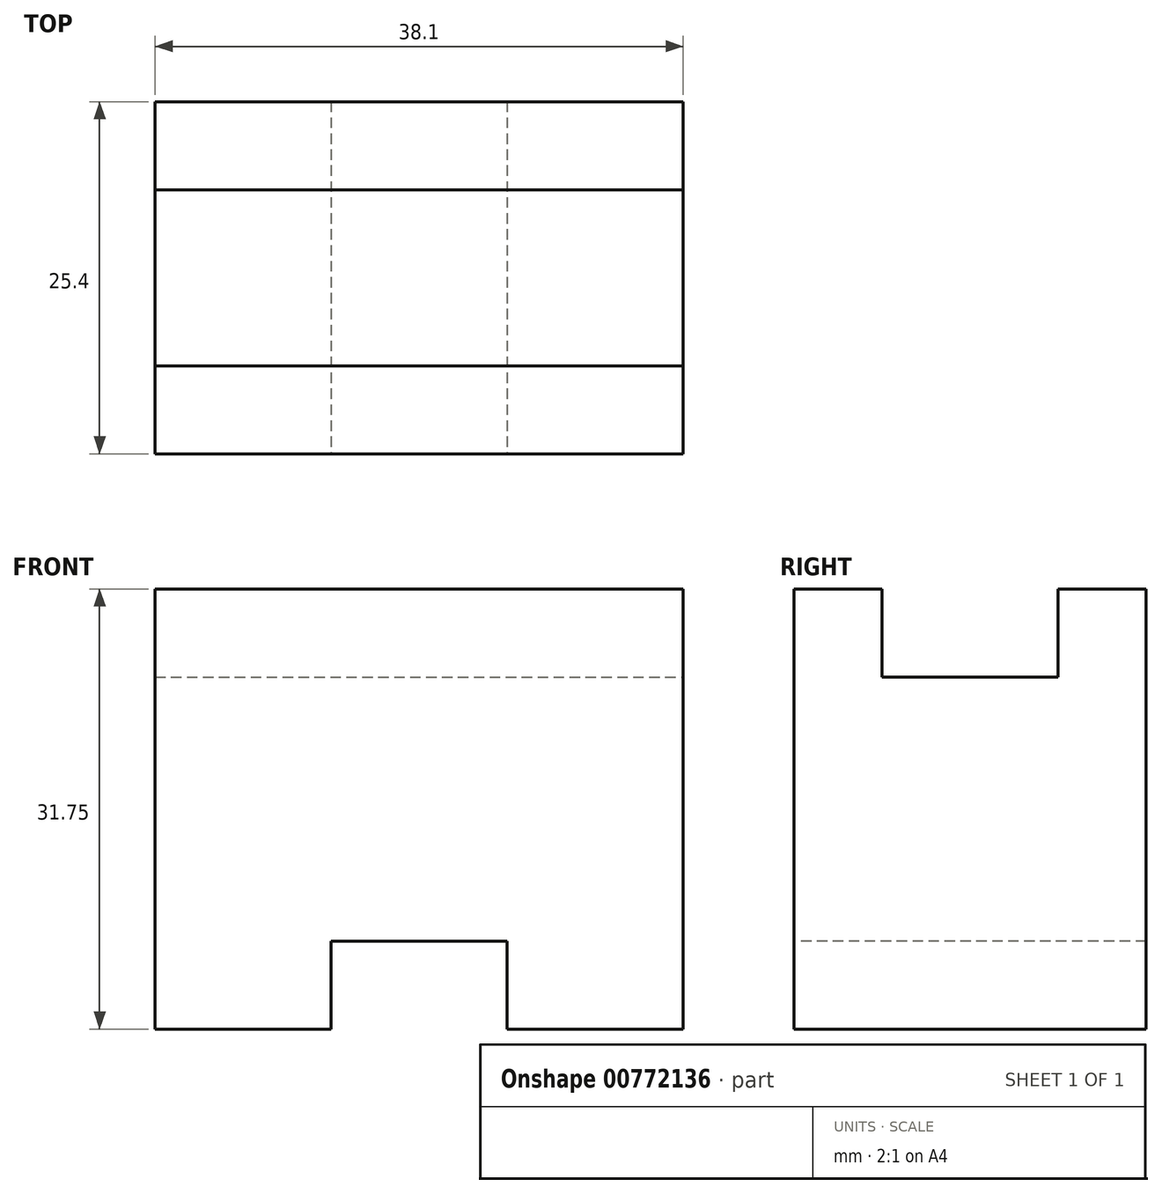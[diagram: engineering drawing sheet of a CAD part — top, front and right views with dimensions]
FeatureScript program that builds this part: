
annotation { "Feature Type Name" : "Feature", "Feature Type Description" : "" }
export const myFeature = defineFeature(function(context is Context, id is Id, definition is map)
    precondition{}
    {
        {
            var Q0;
            Q0=qCreatedBy(makeId("Front.planeOp"),FACE);
            var sketch = newSketch(context, id + "F0", { "sketchPlane" : qUnion([Q0])});
            skLineSegment(sketch, "E0", {"start": v(0, 0) * mm, "end": v(38.1, 0) * mm});
            skLineSegment(sketch, "E1", {"start": v(38.1, 0) * mm, "end": v(38.1, 31.75) * mm});
            skLineSegment(sketch, "E2", {"start": v(38.1, 31.75) * mm, "end": v(0, 31.75) * mm});
            skLineSegment(sketch, "E3", {"start": v(0, 31.75) * mm, "end": v(0, 0) * mm});
            skSolve(sketch);
        }
        {
            var Q0;
            Q0 = qSketchRegion(id + "F0", true);
            extrude(context, id + "F1", {"entities" : qUnion([Q0]), "depth" : 25.4 * mm, "offsetDistance" : 25.4 * mm});
        }
        {
            var Q0;
            Q0=makeQuery(id+"F1.opExtrude","CAP_FACE",FACE,{"disambiguationData":[OSD([sQuery(id+"F0.wireOp",EDGE,"E0"),sQuery(id+"F0.wireOp",EDGE,"E1"),sQuery(id+"F0.wireOp",EDGE,"E2"),sQuery(id+"F0.wireOp",EDGE,"E3")])],"isStart":false});
            var sketch = newSketch(context, id + "F2", { "sketchPlane" : qUnion([Q0])});
            skLineSegment(sketch, "E4", {"start": v(0, 0) * mm, "end": v(12.7, 0) * mm});
            skLineSegment(sketch, "E5", {"start": v(12.7, 0) * mm, "end": v(12.7, 6.35) * mm});
            skLineSegment(sketch, "E6", {"start": v(12.7, 6.35) * mm, "end": v(25.4, 6.35) * mm});
            skLineSegment(sketch, "E7", {"start": v(25.4, 6.35) * mm, "end": v(25.4, 0) * mm});
            skLineSegment(sketch, "E8", {"start": v(25.4, 0) * mm, "end": v(38.1, 0) * mm});
            skSolve(sketch);
        }
        {
            var Q0;
            {var subQ0=sQuery(id+"F2.wireOp",EDGE,"E5");Q0=makeQuery(id+"F2.imprint","IMPRINT",FACE,{"disambiguationData":[TD([[makeQuery(id+"F2.imprint","IMPRINT",EDGE,{"derivedFrom":subQ0}),-1.0]])]});}
            extrude(context, id + "F3", {"entities" : qUnion([Q0]), "operationType" : NewBodyOperationType.REMOVE, "oppositeDirection" : true, "depth" : 25.4 * mm, "offsetDistance" : 25.4 * mm});
        }
        {
            var Q0;
            Q0=makeQuery(id+"F1.opExtrude","SWEPT_FACE",FACE,{"disambiguationData":[OSD([sQuery(id+"F0.wireOp",EDGE,"E1")])]});
            var sketch = newSketch(context, id + "F4", { "sketchPlane" : qUnion([Q0])});
            skLineSegment(sketch, "E9", {"start": v(-25.4, 31.75) * mm, "end": v(-19.05, 31.75) * mm});
            skLineSegment(sketch, "E10", {"start": v(-19.05, 31.75) * mm, "end": v(-19.05, 25.4) * mm});
            skLineSegment(sketch, "E11", {"start": v(-19.05, 25.4) * mm, "end": v(-6.35, 25.4) * mm});
            skLineSegment(sketch, "E12", {"start": v(-6.35, 25.4) * mm, "end": v(-6.35, 31.75) * mm});
            skPoint(sketch, "E12.endSnap0", {"position": v(-22.23, 31.75) * mm});
            skLineSegment(sketch, "E13", {"start": v(-6.35, 31.75) * mm, "end": v(0, 31.75) * mm});
            skSolve(sketch);
        }
        {
            var Q0;
            {var subQ0=sQuery(id+"F4.wireOp",EDGE,"E10");Q0=makeQuery(id+"F4.imprint","IMPRINT",FACE,{"disambiguationData":[TD([[makeQuery(id+"F4.imprint","IMPRINT",EDGE,{"derivedFrom":subQ0}),1.0]])]});}
            extrude(context, id + "F5", {"entities" : qUnion([Q0]), "operationType" : NewBodyOperationType.REMOVE, "oppositeDirection" : true, "depth" : 38.1 * mm, "offsetDistance" : 25.4 * mm});
        }
    });
